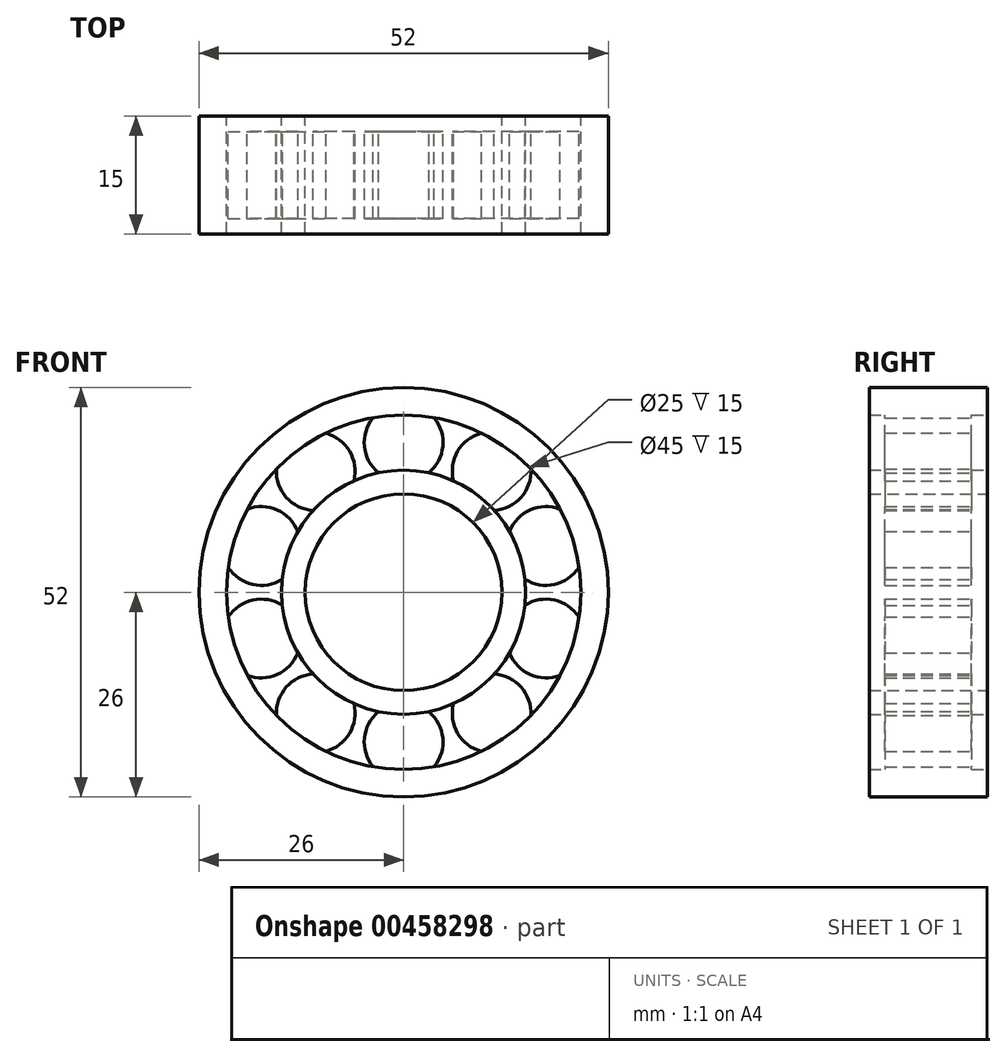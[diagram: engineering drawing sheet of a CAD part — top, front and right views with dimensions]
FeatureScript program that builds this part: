
annotation { "Feature Type Name" : "Feature", "Feature Type Description" : "" }
export const myFeature = defineFeature(function(context is Context, id is Id, definition is map)
    precondition{}
    {
        {
            var Q0;
            Q0=qCreatedBy(makeId("Front.planeOp"),FACE);
            var sketch = newSketch(context, id + "F0", { "sketchPlane" : qUnion([Q0])});
            skCircle(sketch, "E0", {"center": v(0, 0) * mm, "radius": 15.5 * mm});
            skCircle(sketch, "E1", {"center": v(0, 0) * mm, "radius": 12.5 * mm});
            skCircle(sketch, "E2", {"center": v(0, 0) * mm, "radius": 26 * mm});
            skCircle(sketch, "E3", {"center": v(0, 0) * mm, "radius": 22.5 * mm});
            skSolve(sketch);
        }
        {
            var Q0;
            Q0=makeQuery(id+"F0.imprint","IMPRINT",FACE,{"disambiguationData":[TD([[makeQuery(id+"F0.imprint","IMPRINT",EDGE,{"derivedFrom":sQuery(id+"F0.wireOp",EDGE,"E0")}),1.0]])]});
            var Q1;
            Q1=makeQuery(id+"F0.imprint","IMPRINT",FACE,{"disambiguationData":[TD([[makeQuery(id+"F0.imprint","IMPRINT",EDGE,{"derivedFrom":sQuery(id+"F0.wireOp",EDGE,"E2")}),1.0]])]});
            extrude(context, id + "F1", {"entities" : qUnion([Q0, Q1]), "depth" : 15 * mm});
        }
        {
            var Q0;
            Q0=qCreatedBy(makeId("Front.planeOp"),FACE);
            cPlane(context, id + "F2", {"entities" : qUnion([Q0]), "cplaneType" : CPlaneType.OFFSET, "offset" : 7.5 * mm, "width" : 150 * mm, "height" : 150 * mm});
        }
        {
            var Q0;
            Q0=qCreatedBy(id+"F2.planeOp",FACE);
            var sketch = newSketch(context, id + "F3", { "sketchPlane" : qUnion([Q0])});
            skCircle(sketch, "E4", {"center": v(0, 19.02) * mm, "radius": 5 * mm});
            skCircle(sketch, "E5.1.0", {"center": v(-11.18, 15.38) * mm, "radius": 5 * mm});
            skCircle(sketch, "E5.2.0", {"center": v(-18.08, 5.88) * mm, "radius": 5 * mm});
            skCircle(sketch, "E5.3.0", {"center": v(-18.08, -5.88) * mm, "radius": 5 * mm});
            skCircle(sketch, "E5.4.0", {"center": v(-11.18, -15.38) * mm, "radius": 5 * mm});
            skCircle(sketch, "E5.5.0", {"center": v(0, -19.02) * mm, "radius": 5 * mm});
            skCircle(sketch, "E5.6.0", {"center": v(11.18, -15.38) * mm, "radius": 5 * mm});
            skCircle(sketch, "E5.7.0", {"center": v(18.08, -5.88) * mm, "radius": 5 * mm});
            skCircle(sketch, "E5.8.0", {"center": v(18.08, 5.88) * mm, "radius": 5 * mm});
            skCircle(sketch, "E5.9.0", {"center": v(11.18, 15.38) * mm, "radius": 5 * mm});
            skPoint(sketch, "E5.center", {"position": v(0, 0) * mm});
            skSolve(sketch);
        }
        {
            var Q0;
            Q0=makeQuery(id+"F3.imprint","IMPRINT",FACE,{"disambiguationData":[TD([[makeQuery(id+"F3.imprint","IMPRINT",EDGE,{"derivedFrom":sQuery(id+"F3.wireOp",EDGE,"E5.9.0")}),1.0]])]});
            var Q1;
            Q1=makeQuery(id+"F3.imprint","IMPRINT",FACE,{"disambiguationData":[TD([[makeQuery(id+"F3.imprint","IMPRINT",EDGE,{"derivedFrom":sQuery(id+"F3.wireOp",EDGE,"E4")}),1.0]])]});
            var Q2;
            Q2=makeQuery(id+"F3.imprint","IMPRINT",FACE,{"disambiguationData":[TD([[makeQuery(id+"F3.imprint","IMPRINT",EDGE,{"derivedFrom":sQuery(id+"F3.wireOp",EDGE,"E5.1.0")}),1.0]])]});
            var Q3;
            Q3=makeQuery(id+"F3.imprint","IMPRINT",FACE,{"disambiguationData":[TD([[makeQuery(id+"F3.imprint","IMPRINT",EDGE,{"derivedFrom":sQuery(id+"F3.wireOp",EDGE,"E5.2.0")}),1.0]])]});
            var Q4;
            Q4=makeQuery(id+"F3.imprint","IMPRINT",FACE,{"disambiguationData":[TD([[makeQuery(id+"F3.imprint","IMPRINT",EDGE,{"derivedFrom":sQuery(id+"F3.wireOp",EDGE,"E5.3.0")}),1.0]])]});
            var Q5;
            Q5=makeQuery(id+"F3.imprint","IMPRINT",FACE,{"disambiguationData":[TD([[makeQuery(id+"F3.imprint","IMPRINT",EDGE,{"derivedFrom":sQuery(id+"F3.wireOp",EDGE,"E5.4.0")}),1.0]])]});
            var Q6;
            Q6=makeQuery(id+"F3.imprint","IMPRINT",FACE,{"disambiguationData":[TD([[makeQuery(id+"F3.imprint","IMPRINT",EDGE,{"derivedFrom":sQuery(id+"F3.wireOp",EDGE,"E5.5.0")}),1.0]])]});
            var Q7;
            Q7=makeQuery(id+"F3.imprint","IMPRINT",FACE,{"disambiguationData":[TD([[makeQuery(id+"F3.imprint","IMPRINT",EDGE,{"derivedFrom":sQuery(id+"F3.wireOp",EDGE,"E5.6.0")}),1.0]])]});
            var Q8;
            Q8=makeQuery(id+"F3.imprint","IMPRINT",FACE,{"disambiguationData":[TD([[makeQuery(id+"F3.imprint","IMPRINT",EDGE,{"derivedFrom":sQuery(id+"F3.wireOp",EDGE,"E5.7.0")}),1.0]])]});
            var Q9;
            Q9=makeQuery(id+"F3.imprint","IMPRINT",FACE,{"disambiguationData":[TD([[makeQuery(id+"F3.imprint","IMPRINT",EDGE,{"derivedFrom":sQuery(id+"F3.wireOp",EDGE,"E5.8.0")}),1.0]])]});
            extrude(context, id + "F4", {"entities" : qUnion([Q0, Q1, Q2, Q3, Q4, Q5, Q6, Q7, Q8, Q9]), "operationType" : NewBodyOperationType.ADD, "depth" : 11 * mm, "symmetric" : true});
        }
    });
